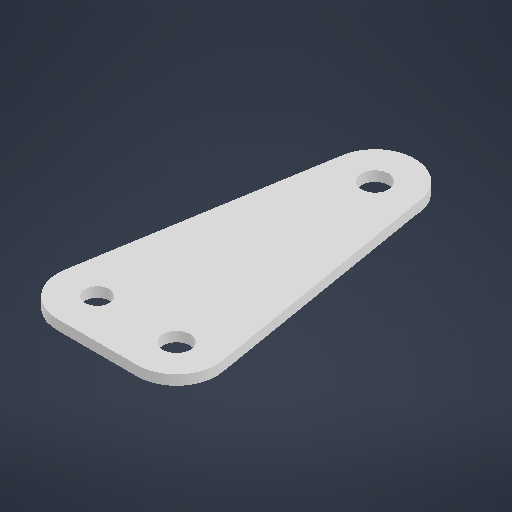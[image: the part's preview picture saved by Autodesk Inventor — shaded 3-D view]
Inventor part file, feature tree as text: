
AUTODESK INVENTOR PART (.ipt)
format: ipt  version: 2025.2 (Build 292293000, 293)  size: 192,000 bytes
history: native  units: in
note: dims shown in document units (in); Inventor stores cm internally (conversion verified against a paired STEP export)
features: extrude x1, sketch x1
ambient origin geometry x8: Origin, YZ Plane, XZ Plane, XY Plane, X Axis, Y Axis, Z Axis, Center Point
bodies: Solid1 (feature_tree)
feature tree (2):
  extrude  "Extrusion1"  Depth=0.5in
  sketch  "Sketch1"  dims[d0=0.172in d1=0.5in d2=0.152in d3=1.5in d4=0.172in d5=0.5in d6=0.5in d7=0.0625in d8=0.0in]
